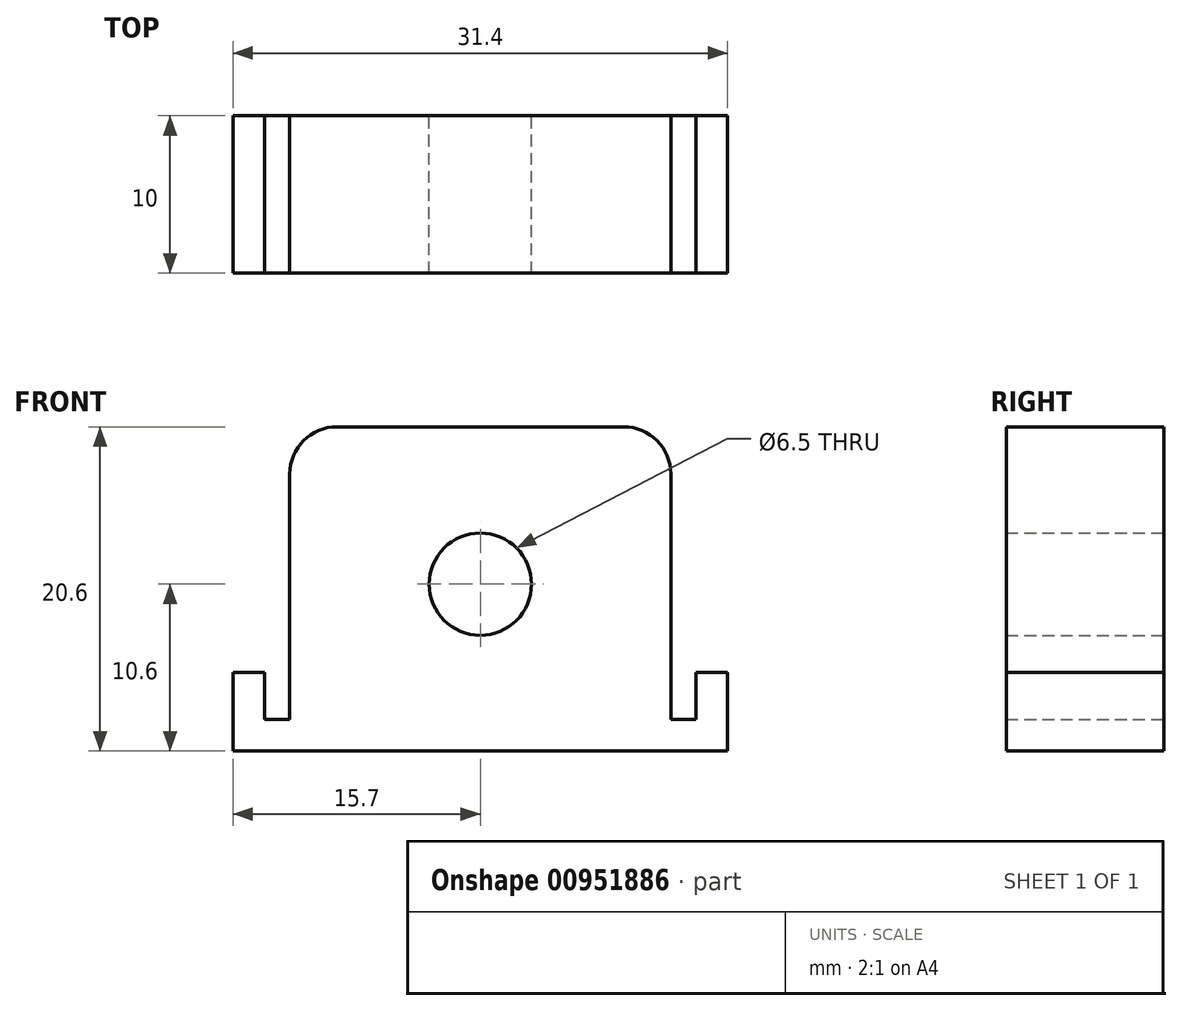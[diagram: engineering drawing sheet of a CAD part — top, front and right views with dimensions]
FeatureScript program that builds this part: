
annotation { "Feature Type Name" : "Feature", "Feature Type Description" : "" }
export const myFeature = defineFeature(function(context is Context, id is Id, definition is map)
    precondition{}
    {
        {
            var Q0;
            Q0=qCreatedBy(makeId("Front.planeOp"),FACE);
            var sketch = newSketch(context, id + "F0", { "sketchPlane" : qUnion([Q0])});
            skLineSegment(sketch, "E0.0", {"start": v(-13.7, -6.54) * mm, "end": v(-13.7, -9.5) * mm});
            skLineSegment(sketch, "E0.2", {"start": v(13.7, -6.54) * mm, "end": v(13.7, -9.5) * mm});
            skLineSegment(sketch, "E1.0", {"start": v(-12.1, 6.05) * mm, "end": v(-12.1, -9.5) * mm});
            skLineSegment(sketch, "E1.1", {"start": v(-9.1, 9.05) * mm, "end": v(9.1, 9.05) * mm});
            skLineSegment(sketch, "E1.2", {"start": v(12.1, 6.05) * mm, "end": v(12.1, -9.5) * mm});
            skArc(sketch, "E2.filletArc", {"start": v(-9.1, 9.05) * mm, "mid": v(-11.22, 8.17) * mm, "end": v(-12.1, 6.05) * mm});
            skArc(sketch, "E3.filletArc", {"start": v(12.1, 6.05) * mm, "mid": v(11.22, 8.17) * mm, "end": v(9.1, 9.05) * mm});
            skLineSegment(sketch, "E4", {"start": v(-13.7, -9.5) * mm, "end": v(-13.7, -9.55) * mm});
            skLineSegment(sketch, "E5", {"start": v(-13.7, -9.55) * mm, "end": v(-12.1, -9.55) * mm});
            skLineSegment(sketch, "E6", {"start": v(-12.1, -9.55) * mm, "end": v(-12.1, -9.5) * mm});
            skLineSegment(sketch, "E7", {"start": v(12.1, -9.5) * mm, "end": v(12.1, -9.55) * mm});
            skLineSegment(sketch, "E8", {"start": v(12.1, -9.55) * mm, "end": v(13.7, -9.55) * mm});
            skLineSegment(sketch, "E9", {"start": v(13.7, -9.55) * mm, "end": v(13.7, -9.5) * mm});
            skLineSegment(sketch, "E10", {"start": v(-13.7, -6.54) * mm, "end": v(-15.7, -6.54) * mm});
            skLineSegment(sketch, "E11", {"start": v(-15.7, -6.54) * mm, "end": v(-15.7, -11.55) * mm});
            skLineSegment(sketch, "E12", {"start": v(13.7, -6.54) * mm, "end": v(15.7, -6.54) * mm});
            skLineSegment(sketch, "E13", {"start": v(15.7, -6.54) * mm, "end": v(15.7, -11.55) * mm});
            skLineSegment(sketch, "E14", {"start": v(-15.7, -11.55) * mm, "end": v(15.7, -11.55) * mm});
            skCircle(sketch, "E15", {"center": v(0, -0.95) * mm, "radius": 3.25 * mm});
            skSolve(sketch);
        }
        {
            var Q0;
            Q0=makeQuery(id+"F0.imprint","IMPRINT",FACE,{"disambiguationData":[TD([[makeQuery(id+"F0.imprint","IMPRINT",EDGE,{"derivedFrom":sQuery(id+"F0.wireOp",EDGE,"E0.0")}),-1.0]])]});
            extrude(context, id + "F1", {"entities" : qUnion([Q0]), "depth" : 10 * mm, "offsetDistance" : 25 * mm});
        }
    });
